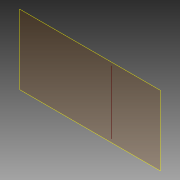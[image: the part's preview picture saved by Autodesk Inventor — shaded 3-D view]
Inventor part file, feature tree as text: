
AUTODESK INVENTOR PART (.ipt)
format: ipt  version: 2013 (Build 170138000, 138)  size: 74,240 bytes
history: native  units: in
note: dims shown in document units (in); Inventor stores cm internally (conversion verified against a paired STEP export)
features: reference x2, plane x1, extrude x1, sketch x1
ambient origin geometry x8: Origin, YZ Plane, XZ Plane, XY Plane, X Axis, Y Axis, Z Axis, Center Point
bodies: Solid1 (feature_tree)
feature tree (5):
  plane  "Work Plane1"
  extrude  "Extrusion1"  Depth=0.1in TaperAngle=0.0deg
  sketch  "Sketch1"  dims[d0=2.0in d2=0.1in d3=0.0in]
  reference  "Reference1"
  reference  "Reference2"
